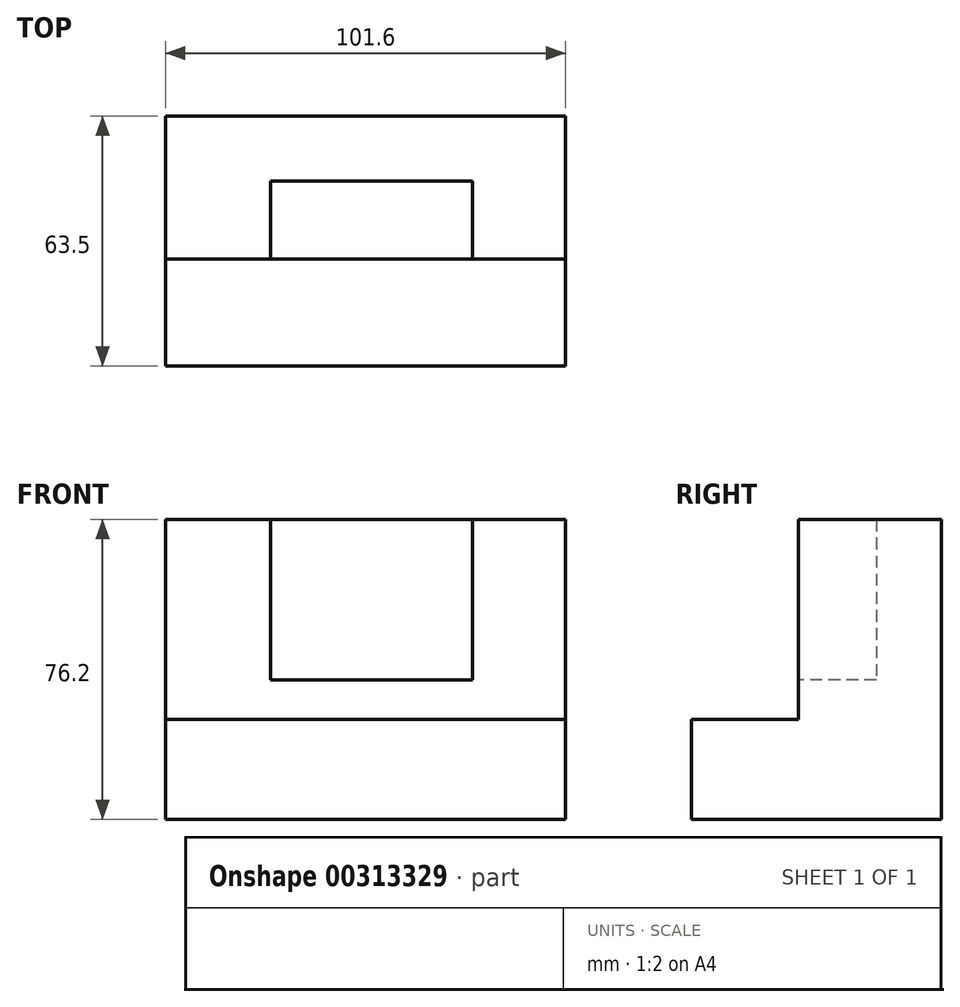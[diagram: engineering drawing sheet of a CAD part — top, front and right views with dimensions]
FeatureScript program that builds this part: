
annotation { "Feature Type Name" : "Feature", "Feature Type Description" : "" }
export const myFeature = defineFeature(function(context is Context, id is Id, definition is map)
    precondition{}
    {
        {
            var Q0;
            Q0=qCreatedBy(makeId("Front.planeOp"),FACE);
            var sketch = newSketch(context, id + "F0", { "sketchPlane" : qUnion([Q0])});
            skLineSegment(sketch, "E0", {"start": v(74.93, -64.12) * mm, "end": v(74.93, -38.72) * mm});
            skLineSegment(sketch, "E1", {"start": v(74.93, -38.72) * mm, "end": v(-26.67, -38.72) * mm});
            skLineSegment(sketch, "E2", {"start": v(-26.67, -38.72) * mm, "end": v(-26.67, -64.12) * mm});
            skLineSegment(sketch, "E3", {"start": v(-26.67, -64.12) * mm, "end": v(74.93, -64.12) * mm});
            skSolve(sketch);
        }
        {
            var Q0;
            Q0=makeQuery(id+"F0.imprint","IMPRINT",FACE,{"disambiguationData":[TD([[makeQuery(id+"F0.imprint","IMPRINT",EDGE,{"derivedFrom":sQuery(id+"F0.wireOp",EDGE,"E0")}),1.0]])]});
            extrude(context, id + "F1", {"entities" : qUnion([Q0]), "depth" : 63.5 * mm});
        }
        {
            var Q0;
            Q0=makeQuery(id+"F1.opExtrude","SWEPT_FACE",FACE,{"disambiguationData":[OSD([sQuery(id+"F0.wireOp",EDGE,"E1")])]});
            var sketch = newSketch(context, id + "F2", { "sketchPlane" : qUnion([Q0])});
            skLineSegment(sketch, "E4", {"start": v(-26.67, -36.32) * mm, "end": v(74.93, -36.32) * mm});
            skLineSegment(sketch, "E5", {"start": v(74.93, -36.32) * mm, "end": v(74.93, 0) * mm});
            skLineSegment(sketch, "E6", {"start": v(74.93, 0) * mm, "end": v(-26.67, 0) * mm});
            skLineSegment(sketch, "E7", {"start": v(-26.67, 0) * mm, "end": v(-26.67, -36.32) * mm});
            skSolve(sketch);
        }
        {
            var Q0;
            Q0=makeQuery(id+"F2.imprint","IMPRINT",FACE,{"disambiguationData":[TD([[makeQuery(id+"F2.imprint","IMPRINT",EDGE,{"derivedFrom":sQuery(id+"F2.wireOp",EDGE,"E4")}),1.0]])]});
            extrude(context, id + "F3", {"entities" : qUnion([Q0]), "operationType" : NewBodyOperationType.ADD, "depth" : 50.8 * mm});
        }
        {
            var Q0;
            Q0=makeQuery(id+"F3.opExtrude","SWEPT_FACE",FACE,{"disambiguationData":[OSD([sQuery(id+"F2.wireOp",EDGE,"E4")])]});
            var sketch = newSketch(context, id + "F4", { "sketchPlane" : qUnion([Q0])});
            skLineSegment(sketch, "E8", {"start": v(0, 12.08) * mm, "end": v(0, -28.66) * mm});
            skLineSegment(sketch, "E9", {"start": v(0, -28.66) * mm, "end": v(51.35, -28.66) * mm});
            skLineSegment(sketch, "E10", {"start": v(51.35, -28.66) * mm, "end": v(51.35, 12.08) * mm});
            skSolve(sketch);
        }
        {
            var Q0;
            {var subQ0=sQuery(id+"F4.wireOp",EDGE,"E8");Q0=makeQuery(id+"F4.imprint","IMPRINT",FACE,{"disambiguationData":[TD([[makeQuery(id+"F4.imprint","IMPRINT",EDGE,{"derivedFrom":subQ0}),1.0]])]});}
            extrude(context, id + "F5", {"entities" : qUnion([Q0]), "operationType" : NewBodyOperationType.REMOVE, "oppositeDirection" : true, "depth" : 19.8 * mm});
        }
    });
